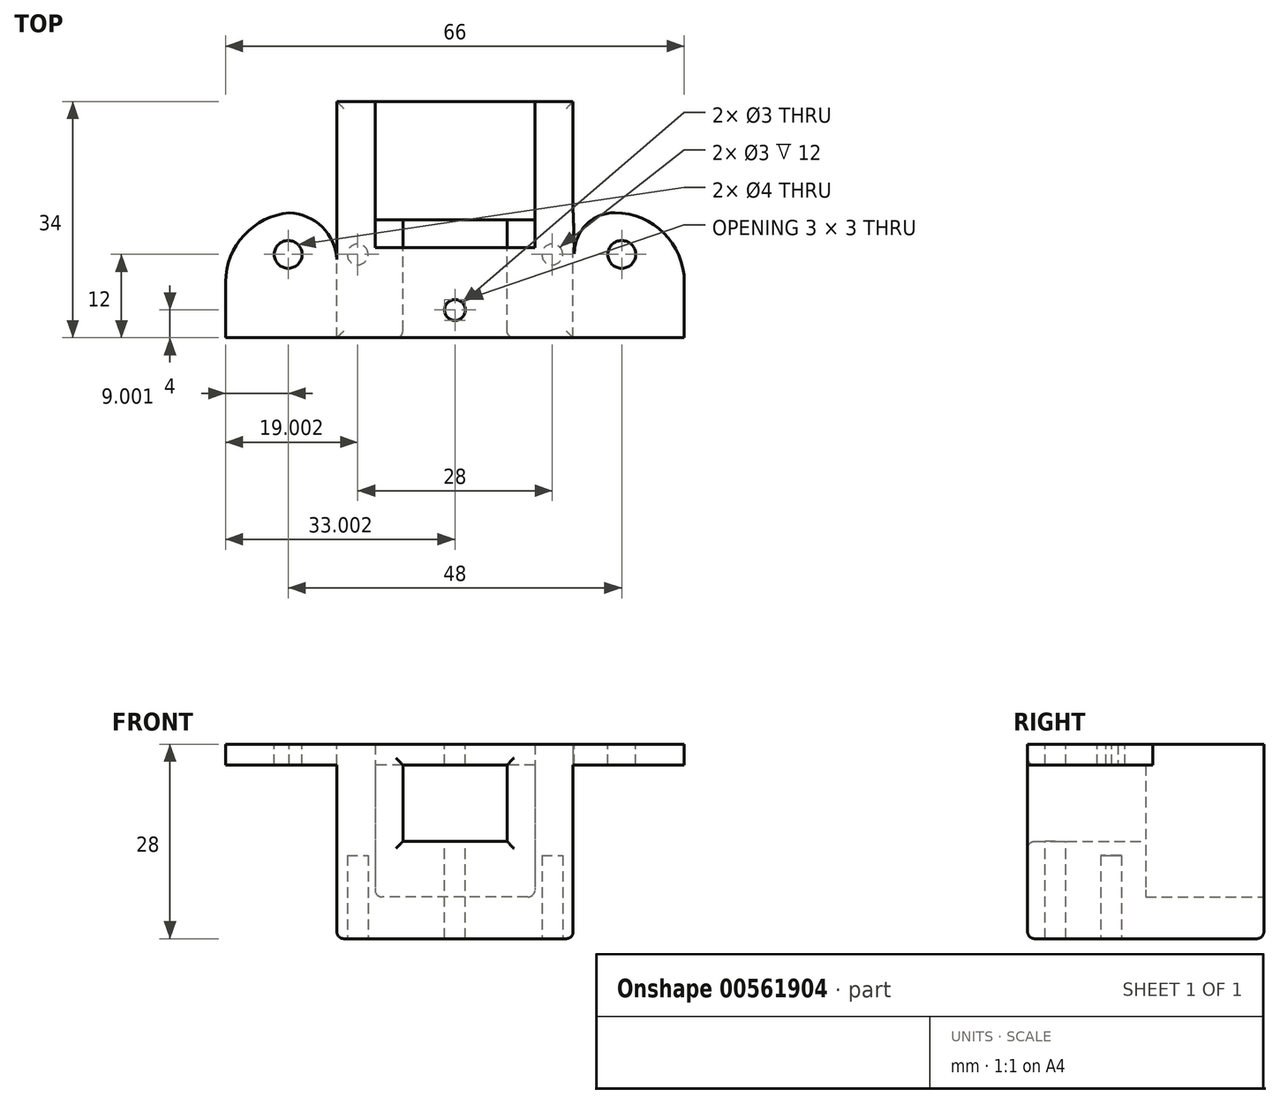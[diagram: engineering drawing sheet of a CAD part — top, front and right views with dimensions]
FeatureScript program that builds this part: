
annotation { "Feature Type Name" : "Feature", "Feature Type Description" : "" }
export const myFeature = defineFeature(function(context is Context, id is Id, definition is map)
    precondition{}
    {
        {
            var Q0;
            Q0=qCreatedBy(makeId("Front.planeOp"),FACE);
            var sketch = newSketch(context, id + "F0", { "sketchPlane" : qUnion([Q0])});
            skLineSegment(sketch, "E0.bottom", {"start": v(-16, 16.61) * mm, "end": v(18, 16.61) * mm});
            skLineSegment(sketch, "E0.top", {"start": v(-16, -11.39) * mm, "end": v(18, -11.39) * mm});
            skLineSegment(sketch, "E0.left", {"start": v(-16, 16.61) * mm, "end": v(-16, -11.39) * mm});
            skLineSegment(sketch, "E0.right", {"start": v(18, 16.61) * mm, "end": v(18, -11.39) * mm});
            skSolve(sketch);
        }
        {
            var Q0;
            Q0=makeQuery(id+"F0.imprint","IMPRINT",FACE,{"disambiguationData":[TD([[makeQuery(id+"F0.imprint","IMPRINT",EDGE,{"derivedFrom":sQuery(id+"F0.wireOp",EDGE,"E0.bottom")}),-1.0]])]});
            extrude(context, id + "F1", {"entities" : qUnion([Q0]), "depth" : 34 * mm, "offsetDistance" : 25 * mm});
        }
        {
            var Q0;
            Q0=makeQuery(id+"F1.opExtrude","SWEPT_FACE",FACE,{"disambiguationData":[OSD([sQuery(id+"F0.wireOp",EDGE,"E0.bottom")])]});
            var sketch = newSketch(context, id + "F2", { "sketchPlane" : qUnion([Q0])});
            skCircle(sketch, "E1", {"center": v(1, -30) * mm, "radius": 1.5 * mm});
            skSolve(sketch);
        }
        {
            var Q0;
            Q0=makeQuery(id+"F1.opExtrude","SWEPT_FACE",FACE,{"disambiguationData":[OSD([sQuery(id+"F0.wireOp",EDGE,"E0.top")])]});
            var sketch = newSketch(context, id + "F3", { "sketchPlane" : qUnion([Q0])});
            skCircle(sketch, "E2", {"center": v(-13, 22) * mm, "radius": 1.5 * mm});
            skCircle(sketch, "E3.1.0.0", {"center": v(15, 22) * mm, "radius": 1.5 * mm});
            skLineSegment(sketch, "E3.direction1", {"start": v(-13, 22) * mm, "end": v(15, 22) * mm, "construction": true});
            skSolve(sketch);
        }
        {
            var Q0;
            Q0=makeQuery(id+"F3.imprint","IMPRINT",FACE,{"disambiguationData":[TD([[makeQuery(id+"F3.imprint","IMPRINT",EDGE,{"derivedFrom":sQuery(id+"F3.wireOp",EDGE,"E2")}),1.0]])]});
            var Q1;
            Q1=makeQuery(id+"F3.imprint","IMPRINT",FACE,{"disambiguationData":[TD([[makeQuery(id+"F3.imprint","IMPRINT",EDGE,{"derivedFrom":sQuery(id+"F3.wireOp",EDGE,"E3.1.0.0")}),1.0]])]});
            extrude(context, id + "F4", {"entities" : qUnion([Q0, Q1]), "operationType" : NewBodyOperationType.REMOVE, "oppositeDirection" : true, "depth" : 12 * mm, "offsetDistance" : 25 * mm});
        }
        {
            var Q0;
            Q0=makeQuery(id+"F1.opExtrude","CAP_FACE",FACE,{"disambiguationData":[OSD([sQuery(id+"F0.wireOp",EDGE,"E0.bottom"),sQuery(id+"F0.wireOp",EDGE,"E0.top"),sQuery(id+"F0.wireOp",EDGE,"E0.left"),sQuery(id+"F0.wireOp",EDGE,"E0.right")])],"isStart":true});
            var sketch = newSketch(context, id + "F5", { "sketchPlane" : qUnion([Q0])});
            skLineSegment(sketch, "E4.bottom", {"start": v(-12.5, 16.61) * mm, "end": v(10.5, 16.61) * mm});
            skLineSegment(sketch, "E4.top", {"start": v(-12.5, -5.39) * mm, "end": v(10.5, -5.39) * mm});
            skLineSegment(sketch, "E4.left", {"start": v(-12.5, 16.61) * mm, "end": v(-12.5, -5.39) * mm});
            skLineSegment(sketch, "E4.right", {"start": v(10.5, 16.61) * mm, "end": v(10.5, -5.39) * mm});
            skLineSegment(sketch, "E5.bottom", {"start": v(-5, -5.39) * mm, "end": v(3, -5.39) * mm});
            skLineSegment(sketch, "E5.top", {"start": v(-5, -15.39) * mm, "end": v(3, -15.39) * mm});
            skLineSegment(sketch, "E5.left", {"start": v(-5, -5.39) * mm, "end": v(-5, -15.39) * mm});
            skLineSegment(sketch, "E5.right", {"start": v(3, -5.39) * mm, "end": v(3, -15.39) * mm});
            skSolve(sketch);
        }
        {
            var Q0;
            Q0=makeQuery(id+"F5.imprint","IMPRINT",FACE,{"disambiguationData":[TD([[makeQuery(id+"F5.imprint","IMPRINT",EDGE,{"derivedFrom":sQuery(id+"F5.wireOp",EDGE,"E4.bottom")}),1.0]])]});
            var Q1;
            {var subQ0=sQuery(id+"F5.wireOp",EDGE,"E5.bottom");Q1=makeQuery(id+"F5.imprint","IMPRINT",FACE,{"disambiguationData":[TD([[makeQuery(id+"F5.imprint","IMPRINT",EDGE,{"derivedFrom":subQ0}),-1.0]])]});}
            extrude(context, id + "F6", {"entities" : qUnion([Q0, Q1]), "operationType" : NewBodyOperationType.REMOVE, "oppositeDirection" : true, "depth" : 17 * mm, "offsetDistance" : 25 * mm});
        }
        {
            var Q0;
            Q0=makeQuery(id+"F2.imprint","IMPRINT",FACE,{"disambiguationData":[TD([[makeQuery(id+"F2.imprint","IMPRINT",EDGE,{"derivedFrom":sQuery(id+"F2.wireOp",EDGE,"E1")}),1.0]])]});
            extrude(context, id + "F7", {"entities" : qUnion([Q0]), "operationType" : NewBodyOperationType.REMOVE, "endBound" : BoundingType.THROUGH_ALL, "oppositeDirection" : true, "depth" : 25 * mm, "offsetDistance" : 25 * mm});
        }
        {
            var Q0;
            Q0=makeQuery(id+"F6.boolean.opBoolean","COPY",FACE,{"derivedFrom":makeQuery(id+"F6.opExtrude","CAP_FACE",FACE,{"disambiguationData":[OSD([sQuery(id+"F0.wireOp",EDGE,"E0.top"),sQuery(id+"F5.wireOp",EDGE,"E4.bottom"),sQuery(id+"F5.wireOp",EDGE,"E4.top"),sQuery(id+"F5.wireOp",EDGE,"E4.left"),sQuery(id+"F5.wireOp",EDGE,"E4.right"),sQuery(id+"F5.wireOp",EDGE,"E5.left"),sQuery(id+"F5.wireOp",EDGE,"E5.right")])],"isStart":false})});
            var sketch = newSketch(context, id + "F8", { "sketchPlane" : qUnion([Q0])});
            skLineSegment(sketch, "E6.bottom", {"start": v(-12.5, 16.61) * mm, "end": v(10.5, 16.61) * mm});
            skLineSegment(sketch, "E6.top", {"start": v(-12.5, 13.61) * mm, "end": v(10.5, 13.61) * mm});
            skLineSegment(sketch, "E6.left", {"start": v(-12.5, 16.61) * mm, "end": v(-12.5, 13.61) * mm});
            skLineSegment(sketch, "E6.right", {"start": v(10.5, 16.61) * mm, "end": v(10.5, 13.61) * mm});
            skSolve(sketch);
        }
        {
            var Q0;
            {var subQ7=sQuery(id+"F8.wireOp",EDGE,"E6.bottom");Q0=makeQuery(id+"F8.imprint","IMPRINT",FACE,{"disambiguationData":[TD([[makeQuery(id+"F8.imprint","IMPRINT",EDGE,{"derivedFrom":subQ7}),1.0]])]});}
            extrude(context, id + "F9", {"entities" : qUnion([Q0]), "operationType" : NewBodyOperationType.REMOVE, "oppositeDirection" : true, "depth" : 4 * mm, "offsetDistance" : 25 * mm});
        }
        {
            var Q0;
            {var subQ0=sQuery(id+"F5.wireOp",EDGE,"E5.left");var subQ1=sQuery(id+"F0.wireOp",EDGE,"E0.top");var subQ2=sQuery(id+"F5.wireOp",EDGE,"E5.right");var subQ4=sQuery(id+"F5.wireOp",EDGE,"E4.top");var subQ5=sQuery(id+"F5.wireOp",EDGE,"E4.right");var subQ6=sQuery(id+"F5.wireOp",EDGE,"E4.left");Q0=makeQuery(id+"F9.boolean.opBoolean","SPLIT",FACE,{"disambiguationData":[TD([makeQuery(id+"F1.opExtrude","SWEPT_FACE",FACE,{"disambiguationData":[OSD([subQ1])]})])],"derivedFrom":makeQuery(id+"F6.boolean.opBoolean","COPY",FACE,{"derivedFrom":makeQuery(id+"F6.opExtrude","CAP_FACE",FACE,{"disambiguationData":[OSD([subQ1,sQuery(id+"F5.wireOp",EDGE,"E4.bottom"),subQ4,subQ6,subQ5,subQ0,subQ2])],"isStart":false})})});}
            var sketch = newSketch(context, id + "F10", { "sketchPlane" : qUnion([Q0])});
            skLineSegment(sketch, "E7.bottom", {"start": v(-8.5, 13.61) * mm, "end": v(6.5, 13.61) * mm});
            skLineSegment(sketch, "E7.top", {"start": v(-8.5, 2.61) * mm, "end": v(6.5, 2.61) * mm});
            skLineSegment(sketch, "E7.left", {"start": v(-8.5, 13.61) * mm, "end": v(-8.5, 2.61) * mm});
            skLineSegment(sketch, "E7.right", {"start": v(6.5, 13.61) * mm, "end": v(6.5, 2.61) * mm});
            skSolve(sketch);
        }
        {
            var Q0;
            Q0=makeQuery(id+"F10.imprint","IMPRINT",FACE,{"disambiguationData":[TD([[makeQuery(id+"F10.imprint","IMPRINT",EDGE,{"derivedFrom":sQuery(id+"F10.wireOp",EDGE,"E7.bottom")}),-1.0]])]});
            extrude(context, id + "F11", {"entities" : qUnion([Q0]), "operationType" : NewBodyOperationType.REMOVE, "endBound" : BoundingType.THROUGH_ALL, "oppositeDirection" : true, "depth" : 25 * mm, "offsetDistance" : 25 * mm});
        }
        {
            var Q0;
            Q0=makeQuery(id+"F1.opExtrude","SWEPT_FACE",FACE,{"disambiguationData":[OSD([sQuery(id+"F0.wireOp",EDGE,"E0.left")])]});
            var sketch = newSketch(context, id + "F12", { "sketchPlane" : qUnion([Q0])});
            skLineSegment(sketch, "E8.bottom", {"start": v(34, 13.61) * mm, "end": v(16, 13.61) * mm});
            skLineSegment(sketch, "E8.top", {"start": v(34, 16.61) * mm, "end": v(16, 16.61) * mm});
            skLineSegment(sketch, "E8.left", {"start": v(34, 13.61) * mm, "end": v(34, 16.61) * mm});
            skLineSegment(sketch, "E8.right", {"start": v(16, 13.61) * mm, "end": v(16, 16.61) * mm});
            skSolve(sketch);
        }
        {
            var Q0;
            Q0=makeQuery(id+"F12.imprint","IMPRINT",FACE,{"disambiguationData":[TD([[makeQuery(id+"F12.imprint","IMPRINT",EDGE,{"derivedFrom":sQuery(id+"F12.wireOp",EDGE,"E8.bottom")}),-1.0]])]});
            extrude(context, id + "F13", {"entities" : qUnion([Q0]), "operationType" : NewBodyOperationType.ADD, "depth" : 16 * mm, "offsetDistance" : 25 * mm});
        }
        {
            var Q0;
            Q0=makeQuery(id+"F1.opExtrude","SWEPT_FACE",FACE,{"disambiguationData":[OSD([sQuery(id+"F0.wireOp",EDGE,"E0.right")])]});
            var sketch = newSketch(context, id + "F14", { "sketchPlane" : qUnion([Q0])});
            skLineSegment(sketch, "E9.bottom", {"start": v(-34, 16.61) * mm, "end": v(-16, 16.61) * mm});
            skLineSegment(sketch, "E9.top", {"start": v(-34, 13.61) * mm, "end": v(-16, 13.61) * mm});
            skLineSegment(sketch, "E9.left", {"start": v(-34, 16.61) * mm, "end": v(-34, 13.61) * mm});
            skLineSegment(sketch, "E9.right", {"start": v(-16, 16.61) * mm, "end": v(-16, 13.61) * mm});
            skSolve(sketch);
        }
        {
            var Q0;
            Q0=makeQuery(id+"F14.imprint","IMPRINT",FACE,{"disambiguationData":[TD([[makeQuery(id+"F14.imprint","IMPRINT",EDGE,{"derivedFrom":sQuery(id+"F14.wireOp",EDGE,"E9.bottom")}),-1.0]])]});
            extrude(context, id + "F15", {"entities" : qUnion([Q0]), "operationType" : NewBodyOperationType.ADD, "depth" : 16 * mm, "offsetDistance" : 25 * mm});
        }
        {
            var Q0;
            Q0=makeQuery(id+"F15.opExtrude","CAP_EDGE",EDGE,{"disambiguationData":[OSD([sQuery(id+"F14.wireOp",EDGE,"E9.right")])],"isStart":false});
            var Q1;
            Q1=makeQuery(id+"F13.opExtrude","CAP_EDGE",EDGE,{"disambiguationData":[OSD([sQuery(id+"F12.wireOp",EDGE,"E8.right")])],"isStart":false});
            fillet(context, id + "F16", {"entities" : qUnion([Q0, Q1]), "radius" : 10 * mm, "tangentPropagation" : true, "allowEdgeOverflow" : false});
        }
        {
            var Q0;
            Q0=makeQuery(id+"F15.boolean.opBoolean","MERGE",FACE,{"derivedFrom":[makeQuery(id+"F13.boolean.opBoolean","MERGE",FACE,{"derivedFrom":[makeQuery(id+"F1.opExtrude","SWEPT_FACE",FACE,{"disambiguationData":[OSD([sQuery(id+"F0.wireOp",EDGE,"E0.bottom")])]}),makeQuery(id+"F13.opExtrude","SWEPT_FACE",FACE,{"disambiguationData":[OSD([sQuery(id+"F12.wireOp",EDGE,"E8.top")])]})]}),makeQuery(id+"F15.opExtrude","SWEPT_FACE",FACE,{"disambiguationData":[OSD([sQuery(id+"F14.wireOp",EDGE,"E9.bottom")])]})]});
            var sketch = newSketch(context, id + "F17", { "sketchPlane" : qUnion([Q0])});
            skCircle(sketch, "E10", {"center": v(-23, -22) * mm, "radius": 2 * mm});
            skCircle(sketch, "E11", {"center": v(25, -22) * mm, "radius": 2 * mm});
            skLineSegment(sketch, "E12", {"start": v(-16, -13.7) * mm, "end": v(-16, -34) * mm});
            skArc(sketch, "E13", {"start": v(-16, -22.74) * mm, "mid": v(-18.11, -18.05) * mm, "end": v(-22.84, -16.03) * mm});
            skLineSegment(sketch, "E14", {"start": v(18, -15.42) * mm, "end": v(18.5, -34) * mm});
            skArc(sketch, "E15", {"start": v(24, -16) * mm, "mid": v(19.84, -17.74) * mm, "end": v(18.17, -21.92) * mm});
            skSolve(sketch);
        }
        {
            var Q0;
            Q0=makeQuery(id+"F17.imprint","IMPRINT",FACE,{"disambiguationData":[TD([[makeQuery(id+"F17.imprint","IMPRINT",EDGE,{"derivedFrom":sQuery(id+"F17.wireOp",EDGE,"E10")}),1.0]])]});
            var Q1;
            Q1=makeQuery(id+"F17.imprint","IMPRINT",FACE,{"disambiguationData":[TD([[makeQuery(id+"F17.imprint","IMPRINT",EDGE,{"derivedFrom":sQuery(id+"F17.wireOp",EDGE,"E11")}),1.0]])]});
            var Q2;
            {var subQ5=sQuery(id+"F17.wireOp",EDGE,"E13");Q2=makeQuery(id+"F17.imprint","IMPRINT",FACE,{"disambiguationData":[TD([[makeQuery(id+"F17.imprint","IMPRINT",EDGE,{"derivedFrom":subQ5}),-1.0]])]});}
            var Q3;
            {var subQ0=sQuery(id+"F17.wireOp",EDGE,"E15");Q3=makeQuery(id+"F17.imprint","IMPRINT",FACE,{"disambiguationData":[TD([[makeQuery(id+"F17.imprint","IMPRINT",EDGE,{"derivedFrom":subQ0}),-1.0]])]});}
            extrude(context, id + "F18", {"entities" : qUnion([Q0, Q1, Q2, Q3]), "operationType" : NewBodyOperationType.REMOVE, "oppositeDirection" : true, "depth" : 25 * mm, "offsetDistance" : 25 * mm});
        }
        {
            var Q0;
            Q0=makeQuery(id+"F1.opExtrude","SWEPT_EDGE",EDGE,{"disambiguationData":[OSD([sQuery(id+"F0.wireOp",EDGE,"E0.top"),sQuery(id+"F0.wireOp",EDGE,"E0.left")])]});
            var Q1;
            Q1=makeQuery(id+"F1.opExtrude","SWEPT_EDGE",EDGE,{"disambiguationData":[OSD([sQuery(id+"F0.wireOp",EDGE,"E0.top"),sQuery(id+"F0.wireOp",EDGE,"E0.right")])]});
            var Q2;
            Q2=makeQuery(id+"F6.boolean.opBoolean","COPY",EDGE,{"derivedFrom":makeQuery(id+"F6.opExtrude","SWEPT_EDGE",EDGE,{"disambiguationData":[OSD([sQuery(id+"F5.wireOp",EDGE,"E4.top"),sQuery(id+"F5.wireOp",EDGE,"E5.bottom"),sQuery(id+"F5.wireOp",EDGE,"E5.left")])]})});
            var Q3;
            Q3=makeQuery(id+"F6.boolean.opBoolean","COPY",EDGE,{"derivedFrom":makeQuery(id+"F6.opExtrude","SWEPT_EDGE",EDGE,{"disambiguationData":[OSD([sQuery(id+"F5.wireOp",EDGE,"E4.top"),sQuery(id+"F5.wireOp",EDGE,"E5.bottom"),sQuery(id+"F5.wireOp",EDGE,"E5.right")])]})});
            var Q4;
            Q4=makeQuery(id+"F6.boolean.opBoolean","COPY",EDGE,{"derivedFrom":makeQuery(id+"F6.opExtrude","SWEPT_EDGE",EDGE,{"disambiguationData":[OSD([sQuery(id+"F0.wireOp",EDGE,"E0.top"),sQuery(id+"F5.wireOp",EDGE,"E5.left")])]})});
            var Q5;
            Q5=makeQuery(id+"F6.boolean.opBoolean","COPY",EDGE,{"derivedFrom":makeQuery(id+"F6.opExtrude","SWEPT_EDGE",EDGE,{"disambiguationData":[OSD([sQuery(id+"F0.wireOp",EDGE,"E0.top"),sQuery(id+"F5.wireOp",EDGE,"E5.right")])]})});
            var Q6;
            Q6=makeQuery(id+"F6.boolean.opBoolean","COPY",EDGE,{"derivedFrom":makeQuery(id+"F6.opExtrude","SWEPT_EDGE",EDGE,{"disambiguationData":[OSD([sQuery(id+"F0.wireOp",EDGE,"E0.bottom"),sQuery(id+"F5.wireOp",EDGE,"E4.bottom"),sQuery(id+"F5.wireOp",EDGE,"E4.left")])]})});
            var Q7;
            Q7=makeQuery(id+"F6.boolean.opBoolean","COPY",EDGE,{"derivedFrom":makeQuery(id+"F6.opExtrude","SWEPT_EDGE",EDGE,{"disambiguationData":[OSD([sQuery(id+"F0.wireOp",EDGE,"E0.bottom"),sQuery(id+"F5.wireOp",EDGE,"E4.bottom"),sQuery(id+"F5.wireOp",EDGE,"E4.right")])]})});
            var Q8;
            Q8=makeQuery(id+"F11.boolean.opBoolean","INTERSECT",EDGE,{"derivedFrom":[makeQuery(id+"F1.opExtrude","CAP_FACE",FACE,{"disambiguationData":[OSD([sQuery(id+"F0.wireOp",EDGE,"E0.bottom"),sQuery(id+"F0.wireOp",EDGE,"E0.top"),sQuery(id+"F0.wireOp",EDGE,"E0.left"),sQuery(id+"F0.wireOp",EDGE,"E0.right")])],"isStart":false}),makeQuery(id+"F11.opExtrude","SWEPT_FACE",FACE,{"disambiguationData":[OSD([sQuery(id+"F10.wireOp",EDGE,"E7.top")])]})]});
            var Q9;
            Q9=makeQuery(id+"F11.boolean.opBoolean","INTERSECT",EDGE,{"derivedFrom":[makeQuery(id+"F1.opExtrude","CAP_FACE",FACE,{"disambiguationData":[OSD([sQuery(id+"F0.wireOp",EDGE,"E0.bottom"),sQuery(id+"F0.wireOp",EDGE,"E0.top"),sQuery(id+"F0.wireOp",EDGE,"E0.left"),sQuery(id+"F0.wireOp",EDGE,"E0.right")])],"isStart":false}),makeQuery(id+"F11.opExtrude","SWEPT_FACE",FACE,{"disambiguationData":[OSD([sQuery(id+"F10.wireOp",EDGE,"E7.left")])]})]});
            var Q10;
            Q10=makeQuery(id+"F11.boolean.opBoolean","INTERSECT",EDGE,{"derivedFrom":[makeQuery(id+"F1.opExtrude","CAP_FACE",FACE,{"disambiguationData":[OSD([sQuery(id+"F0.wireOp",EDGE,"E0.bottom"),sQuery(id+"F0.wireOp",EDGE,"E0.top"),sQuery(id+"F0.wireOp",EDGE,"E0.left"),sQuery(id+"F0.wireOp",EDGE,"E0.right")])],"isStart":false}),makeQuery(id+"F11.opExtrude","SWEPT_FACE",FACE,{"disambiguationData":[OSD([sQuery(id+"F10.wireOp",EDGE,"E7.bottom")])]})]});
            var Q11;
            Q11=makeQuery(id+"F11.boolean.opBoolean","INTERSECT",EDGE,{"derivedFrom":[makeQuery(id+"F1.opExtrude","CAP_FACE",FACE,{"disambiguationData":[OSD([sQuery(id+"F0.wireOp",EDGE,"E0.bottom"),sQuery(id+"F0.wireOp",EDGE,"E0.top"),sQuery(id+"F0.wireOp",EDGE,"E0.left"),sQuery(id+"F0.wireOp",EDGE,"E0.right")])],"isStart":false}),makeQuery(id+"F11.opExtrude","SWEPT_FACE",FACE,{"disambiguationData":[OSD([sQuery(id+"F10.wireOp",EDGE,"E7.right")])]})]});
            var Q12;
            {var subQ0=sQuery(id+"F8.wireOp",EDGE,"E6.top");var subQ1=sQuery(id+"F5.wireOp",EDGE,"E4.right");Q12=makeQuery(id+"F11.boolean.opBoolean","SPLIT",EDGE,{"disambiguationData":[TD([makeQuery(id+"F6.boolean.opBoolean","COPY",FACE,{"derivedFrom":makeQuery(id+"F6.opExtrude","SWEPT_FACE",FACE,{"disambiguationData":[OSD([subQ1])]})})])],"derivedFrom":makeQuery(id+"F9.boolean.opBoolean","COPY",EDGE,{"derivedFrom":makeQuery(id+"F9.opExtrude","CAP_EDGE",EDGE,{"disambiguationData":[OSD([subQ0])],"isStart":true})})});}
            var Q13;
            {var subQ0=sQuery(id+"F8.wireOp",EDGE,"E6.top");var subQ1=sQuery(id+"F5.wireOp",EDGE,"E4.left");Q13=makeQuery(id+"F11.boolean.opBoolean","SPLIT",EDGE,{"disambiguationData":[TD([makeQuery(id+"F6.boolean.opBoolean","COPY",FACE,{"derivedFrom":makeQuery(id+"F6.opExtrude","SWEPT_FACE",FACE,{"disambiguationData":[OSD([subQ1])]})})])],"derivedFrom":makeQuery(id+"F9.boolean.opBoolean","COPY",EDGE,{"derivedFrom":makeQuery(id+"F9.opExtrude","CAP_EDGE",EDGE,{"disambiguationData":[OSD([subQ0])],"isStart":true})})});}
            var Q14;
            Q14=makeQuery(id+"F1.opExtrude","CAP_EDGE",EDGE,{"disambiguationData":[OSD([sQuery(id+"F0.wireOp",EDGE,"E0.top")])],"isStart":false});
            var Q15;
            {var subQ0=sQuery(id+"F0.wireOp",EDGE,"E0.left");var subQ1=sQuery(id+"F0.wireOp",EDGE,"E0.top");Q15=makeQuery(id+"F6.boolean.opBoolean","SPLIT",EDGE,{"disambiguationData":[TD([makeQuery(id+"F1.opExtrude","SWEPT_FACE",FACE,{"disambiguationData":[OSD([subQ0])]})])],"derivedFrom":makeQuery(id+"F1.opExtrude","CAP_EDGE",EDGE,{"disambiguationData":[OSD([subQ1])],"isStart":true})});}
            var Q16;
            {var subQ0=sQuery(id+"F0.wireOp",EDGE,"E0.right");var subQ1=sQuery(id+"F0.wireOp",EDGE,"E0.top");Q16=makeQuery(id+"F6.boolean.opBoolean","SPLIT",EDGE,{"disambiguationData":[TD([makeQuery(id+"F1.opExtrude","SWEPT_FACE",FACE,{"disambiguationData":[OSD([subQ0])]})])],"derivedFrom":makeQuery(id+"F1.opExtrude","CAP_EDGE",EDGE,{"disambiguationData":[OSD([subQ1])],"isStart":true})});}
            fillet(context, id + "F19", {"entities" : qUnion([Q0, Q1, Q2, Q3, Q4, Q5, Q6, Q7, Q8, Q9, Q10, Q11, Q12, Q13, Q14, Q15, Q16]), "radius" : 1 * mm, "tangentPropagation" : true, "allowEdgeOverflow" : false});
        }
    });
